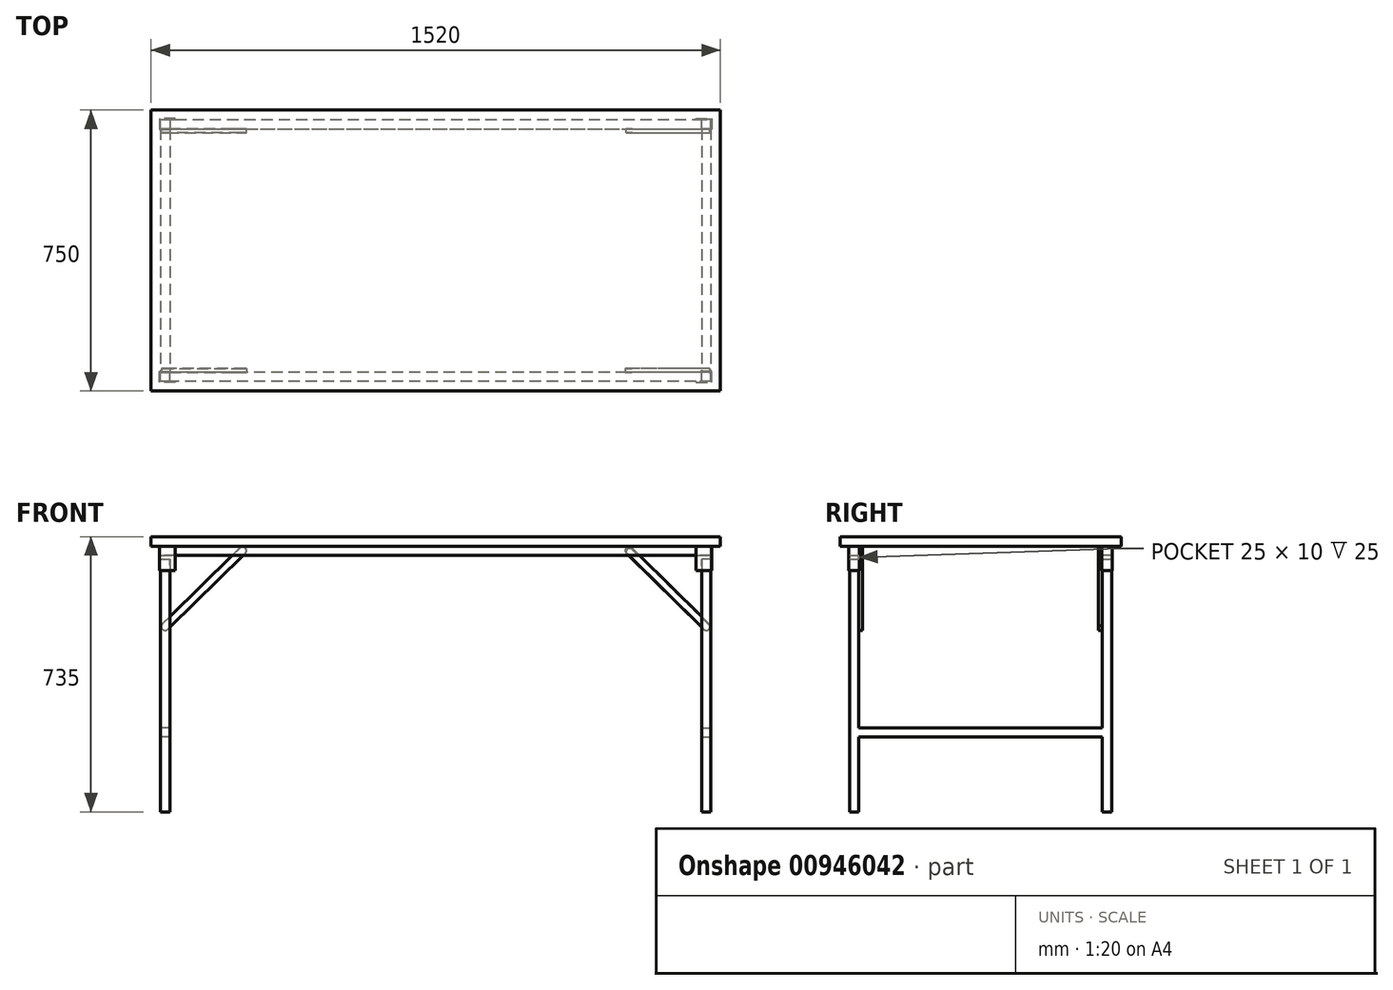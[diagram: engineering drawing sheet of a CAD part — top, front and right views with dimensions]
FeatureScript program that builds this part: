
annotation { "Feature Type Name" : "Feature", "Feature Type Description" : "" }
export const myFeature = defineFeature(function(context is Context, id is Id, definition is map)
    precondition{}
    {
        {
            var Q0;
            Q0=qCreatedBy(makeId("Top.planeOp"),FACE);
            var sketch = newSketch(context, id + "F0", { "sketchPlane" : qUnion([Q0])});
            skLineSegment(sketch, "E0.bottom", {"start": v(0, 0) * mm, "end": v(-1520, 0) * mm});
            skLineSegment(sketch, "E0.top", {"start": v(0, 750) * mm, "end": v(-1520, 750) * mm});
            skLineSegment(sketch, "E0.left", {"start": v(0, 0) * mm, "end": v(0, 750) * mm});
            skLineSegment(sketch, "E0.right", {"start": v(-1520, 0) * mm, "end": v(-1520, 750) * mm});
            skSolve(sketch);
        }
        {
            var Q0;
            Q0=makeQuery(id+"F0.imprint","IMPRINT",FACE,{"disambiguationData":[TD([[makeQuery(id+"F0.imprint","IMPRINT",EDGE,{"derivedFrom":sQuery(id+"F0.wireOp",EDGE,"E0.bottom")}),-1.0]])]});
            extrude(context, id + "F1", {"entities" : qUnion([Q0]), "depth" : 25 * mm, "offsetDistance" : 25 * mm});
        }
        {
            var Q0;
            Q0=makeQuery(id+"F1.opExtrude","CAP_FACE",FACE,{"disambiguationData":[OSD([sQuery(id+"F0.wireOp",EDGE,"E0.bottom"),sQuery(id+"F0.wireOp",EDGE,"E0.top"),sQuery(id+"F0.wireOp",EDGE,"E0.left"),sQuery(id+"F0.wireOp",EDGE,"E0.right")])],"isStart":true});
            var sketch = newSketch(context, id + "F2", { "sketchPlane" : qUnion([Q0])});
            skLineSegment(sketch, "E1.bottom", {"start": v(-25, -25) * mm, "end": v(-1495, -25) * mm});
            skLineSegment(sketch, "E1.top", {"start": v(-25, -50) * mm, "end": v(-1495, -50) * mm});
            skLineSegment(sketch, "E1.left", {"start": v(-25, -25) * mm, "end": v(-25, -50) * mm});
            skLineSegment(sketch, "E1.right", {"start": v(-1495, -25) * mm, "end": v(-1495, -50) * mm});
            skLineSegment(sketch, "E2.bottom", {"start": v(-1495, -700) * mm, "end": v(-25, -700) * mm});
            skLineSegment(sketch, "E2.top", {"start": v(-1495, -725) * mm, "end": v(-25, -725) * mm});
            skLineSegment(sketch, "E2.left", {"start": v(-1495, -700) * mm, "end": v(-1495, -725) * mm});
            skLineSegment(sketch, "E2.right", {"start": v(-25, -700) * mm, "end": v(-25, -725) * mm});
            skSolve(sketch);
        }
        {
            var Q0;
            Q0 = qSketchRegion(id + "F2", true);
            extrude(context, id + "F3", {"entities" : qUnion([Q0]), "operationType" : NewBodyOperationType.ADD, "depth" : 25 * mm, "offsetDistance" : 25 * mm});
        }
        {
            var Q0;
            Q0=makeQuery(id+"F1.opExtrude","CAP_FACE",FACE,{"disambiguationData":[OSD([sQuery(id+"F0.wireOp",EDGE,"E0.bottom"),sQuery(id+"F0.wireOp",EDGE,"E0.top"),sQuery(id+"F0.wireOp",EDGE,"E0.left"),sQuery(id+"F0.wireOp",EDGE,"E0.right")])],"isStart":true});
            var sketch = newSketch(context, id + "F4", { "sketchPlane" : qUnion([Q0])});
            skLineSegment(sketch, "E3", {"start": v(-25, -25) * mm, "end": v(-65, -25) * mm});
            skLineSegment(sketch, "E4", {"start": v(-65, -25) * mm, "end": v(-65, -23) * mm});
            skLineSegment(sketch, "E5", {"start": v(-65, -23) * mm, "end": v(-23, -23) * mm});
            skLineSegment(sketch, "E6", {"start": v(-23, -23) * mm, "end": v(-23, -52) * mm});
            skLineSegment(sketch, "E7", {"start": v(-23, -52) * mm, "end": v(-65, -52) * mm});
            skLineSegment(sketch, "E8", {"start": v(-65, -52) * mm, "end": v(-65, -50) * mm});
            skLineSegment(sketch, "E9", {"start": v(-65, -50) * mm, "end": v(-25, -50) * mm});
            skLineSegment(sketch, "E10", {"start": v(-25, -50) * mm, "end": v(-25, -25) * mm});
            skSolve(sketch);
        }
        {
            var Q0;
            Q0=makeQuery(id+"F4.imprint","IMPRINT",FACE,{"disambiguationData":[TD([[makeQuery(id+"F4.imprint","IMPRINT",EDGE,{"derivedFrom":sQuery(id+"F4.wireOp",EDGE,"E3")}),-1.0]])]});
            extrude(context, id + "F5", {"entities" : qUnion([Q0]), "operationType" : NewBodyOperationType.ADD, "depth" : 65 * mm, "offsetDistance" : 25 * mm});
        }
        {
            var Q0;
            Q0=makeQuery(id+"F3.opExtrude","CAP_FACE",FACE,{"disambiguationData":[OSD([sQuery(id+"F2.wireOp",EDGE,"E1.bottom"),sQuery(id+"F2.wireOp",EDGE,"E1.top"),sQuery(id+"F2.wireOp",EDGE,"E1.left"),sQuery(id+"F2.wireOp",EDGE,"E1.right")])],"isStart":false});
            cPlane(context, id + "F6", {"entities" : qUnion([Q0]), "cplaneType" : CPlaneType.OFFSET, "offset" : 10 * mm, "width" : 150 * mm, "height" : 150 * mm});
        }
        {
            var Q0;
            Q0=qCreatedBy(id+"F6.planeOp",FACE);
            var sketch = newSketch(context, id + "F7", { "sketchPlane" : qUnion([Q0])});
            skLineSegment(sketch, "E11.bottom", {"start": v(-25, -25.02) * mm, "end": v(-50, -25.02) * mm});
            skLineSegment(sketch, "E11.top", {"start": v(-25, -50.02) * mm, "end": v(-50, -50.02) * mm});
            skLineSegment(sketch, "E11.left", {"start": v(-25, -25.02) * mm, "end": v(-25, -50.02) * mm});
            skLineSegment(sketch, "E11.right", {"start": v(-50, -25.02) * mm, "end": v(-50, -50.02) * mm});
            skSolve(sketch);
        }
        {
            var Q0;
            Q0=makeQuery(id+"F7.imprint","IMPRINT",FACE,{"disambiguationData":[TD([[makeQuery(id+"F7.imprint","IMPRINT",EDGE,{"derivedFrom":sQuery(id+"F7.wireOp",EDGE,"E11.bottom")}),1.0]])]});
            extrude(context, id + "F8", {"entities" : qUnion([Q0]), "operationType" : NewBodyOperationType.ADD, "depth" : 675 * mm, "offsetDistance" : 25 * mm});
        }
        {
            var Q0;
            Q0=makeQuery(id+"F0.imprint","IMPRINT",FACE,{"disambiguationData":[TD([[makeQuery(id+"F0.imprint","IMPRINT",EDGE,{"derivedFrom":sQuery(id+"F0.wireOp",EDGE,"E0.bottom")}),-1.0]])]});
            var sketch = newSketch(context, id + "F9", { "sketchPlane" : qUnion([Q0])});
            skLineSegment(sketch, "E12", {"start": v(-1495, 25) * mm, "end": v(-1455, 25) * mm});
            skLineSegment(sketch, "E13", {"start": v(-1455, 25) * mm, "end": v(-1455, 23) * mm});
            skLineSegment(sketch, "E14", {"start": v(-1455, 23) * mm, "end": v(-1497, 23) * mm});
            skLineSegment(sketch, "E15", {"start": v(-1497, 23) * mm, "end": v(-1497, 52) * mm});
            skLineSegment(sketch, "E16", {"start": v(-1497, 52) * mm, "end": v(-1455, 52) * mm});
            skLineSegment(sketch, "E17", {"start": v(-1455, 52) * mm, "end": v(-1455, 50) * mm});
            skLineSegment(sketch, "E18", {"start": v(-1455, 50) * mm, "end": v(-1495, 50) * mm});
            skLineSegment(sketch, "E19", {"start": v(-1495, 50) * mm, "end": v(-1495, 25) * mm});
            skLineSegment(sketch, "E20.MirrorCS", {"start": v(-1455, 724.98) * mm, "end": v(-1455, 726.98) * mm});
            skLineSegment(sketch, "E21.MirrorCS", {"start": v(-1455, 697.98) * mm, "end": v(-1455, 699.98) * mm});
            skLineSegment(sketch, "E22.MirrorCS", {"start": v(-1497, 697.98) * mm, "end": v(-1455, 697.98) * mm});
            skLineSegment(sketch, "E23.MirrorCS", {"start": v(-1455, 699.98) * mm, "end": v(-1495, 699.98) * mm});
            skLineSegment(sketch, "E24.MirrorCS", {"start": v(-1495, 724.98) * mm, "end": v(-1455, 724.98) * mm});
            skLineSegment(sketch, "E25.MirrorCS", {"start": v(-1455, 726.98) * mm, "end": v(-1497, 726.98) * mm});
            skLineSegment(sketch, "E26.MirrorCS", {"start": v(-1497, 726.98) * mm, "end": v(-1497, 697.98) * mm});
            skLineSegment(sketch, "E27.MirrorCS", {"start": v(-1495, 699.98) * mm, "end": v(-1495, 724.98) * mm});
            skLineSegment(sketch, "E28.MirrorCS", {"start": v(-65.05, 724.98) * mm, "end": v(-65.05, 726.98) * mm});
            skLineSegment(sketch, "E29.MirrorCS", {"start": v(-65.05, 697.98) * mm, "end": v(-65.05, 699.98) * mm});
            skLineSegment(sketch, "E30.MirrorCS", {"start": v(-23.05, 726.98) * mm, "end": v(-23.05, 697.98) * mm});
            skLineSegment(sketch, "E31.MirrorCS", {"start": v(-65.05, 699.98) * mm, "end": v(-25.05, 699.98) * mm});
            skLineSegment(sketch, "E32.MirrorCS", {"start": v(-25.05, 699.98) * mm, "end": v(-25.05, 724.98) * mm});
            skLineSegment(sketch, "E33.MirrorCS", {"start": v(-65.05, 726.98) * mm, "end": v(-23.05, 726.98) * mm});
            skLineSegment(sketch, "E34.MirrorCS", {"start": v(-25.05, 724.98) * mm, "end": v(-65.05, 724.98) * mm});
            skLineSegment(sketch, "E35.MirrorCS", {"start": v(-23.05, 697.98) * mm, "end": v(-65.05, 697.98) * mm});
            skSolve(sketch);
        }
        {
            var Q0;
            Q0=makeQuery(id+"F9.imprint","IMPRINT",FACE,{"disambiguationData":[TD([[makeQuery(id+"F9.imprint","IMPRINT",EDGE,{"derivedFrom":sQuery(id+"F9.wireOp",EDGE,"E20.MirrorCS")}),1.0]])]});
            var Q1;
            Q1=makeQuery(id+"F9.imprint","IMPRINT",FACE,{"disambiguationData":[TD([[makeQuery(id+"F9.imprint","IMPRINT",EDGE,{"derivedFrom":sQuery(id+"F9.wireOp",EDGE,"E28.MirrorCS")}),-1.0]])]});
            var Q2;
            Q2=makeQuery(id+"F9.imprint","IMPRINT",FACE,{"disambiguationData":[TD([[makeQuery(id+"F9.imprint","IMPRINT",EDGE,{"derivedFrom":sQuery(id+"F9.wireOp",EDGE,"E12")}),-1.0]])]});
            extrude(context, id + "F10", {"entities" : qUnion([Q0, Q1, Q2]), "operationType" : NewBodyOperationType.ADD, "oppositeDirection" : true, "depth" : 65 * mm, "offsetDistance" : 25 * mm});
        }
        {
            var Q0;
            Q0=makeQuery(id+"F3.opExtrude","CAP_FACE",FACE,{"disambiguationData":[OSD([sQuery(id+"F2.wireOp",EDGE,"E1.bottom"),sQuery(id+"F2.wireOp",EDGE,"E1.top"),sQuery(id+"F2.wireOp",EDGE,"E1.left"),sQuery(id+"F2.wireOp",EDGE,"E1.right")])],"isStart":false});
            cPlane(context, id + "F11", {"entities" : qUnion([Q0]), "cplaneType" : CPlaneType.OFFSET, "offset" : 10 * mm, "width" : 150 * mm, "height" : 150 * mm});
        }
        {
            var Q0;
            Q0=qCreatedBy(id+"F11.planeOp",FACE);
            var sketch = newSketch(context, id + "F12", { "sketchPlane" : qUnion([Q0])});
            skLineSegment(sketch, "E36.bottom", {"start": v(-1470, -25) * mm, "end": v(-1495, -25) * mm});
            skLineSegment(sketch, "E36.top", {"start": v(-1470, -50) * mm, "end": v(-1495, -50) * mm});
            skLineSegment(sketch, "E36.left", {"start": v(-1470, -25) * mm, "end": v(-1470, -50) * mm});
            skLineSegment(sketch, "E36.right", {"start": v(-1495, -25) * mm, "end": v(-1495, -50) * mm});
            skSolve(sketch);
        }
        {
            var Q0;
            Q0=makeQuery(id+"F12.imprint","IMPRINT",FACE,{"disambiguationData":[TD([[makeQuery(id+"F12.imprint","IMPRINT",EDGE,{"derivedFrom":sQuery(id+"F12.wireOp",EDGE,"E36.bottom")}),1.0]])]});
            extrude(context, id + "F13", {"entities" : qUnion([Q0]), "operationType" : NewBodyOperationType.ADD, "depth" : 675 * mm, "offsetDistance" : 25 * mm});
        }
        {
            var Q0;
            Q0=makeQuery(id+"F3.opExtrude","CAP_FACE",FACE,{"disambiguationData":[OSD([sQuery(id+"F2.wireOp",EDGE,"E2.bottom"),sQuery(id+"F2.wireOp",EDGE,"E2.top"),sQuery(id+"F2.wireOp",EDGE,"E2.left"),sQuery(id+"F2.wireOp",EDGE,"E2.right")])],"isStart":false});
            cPlane(context, id + "F14", {"entities" : qUnion([Q0]), "cplaneType" : CPlaneType.OFFSET, "offset" : 10 * mm, "width" : 150 * mm, "height" : 150 * mm});
        }
        {
            var Q0;
            Q0=qCreatedBy(id+"F14.planeOp",FACE);
            var sketch = newSketch(context, id + "F15", { "sketchPlane" : qUnion([Q0])});
            skLineSegment(sketch, "E37.bottom", {"start": v(-25, -700) * mm, "end": v(-50, -700) * mm});
            skLineSegment(sketch, "E37.top", {"start": v(-25, -725) * mm, "end": v(-50, -725) * mm});
            skLineSegment(sketch, "E37.left", {"start": v(-25, -700) * mm, "end": v(-25, -725) * mm});
            skLineSegment(sketch, "E37.right", {"start": v(-50, -700) * mm, "end": v(-50, -725) * mm});
            skLineSegment(sketch, "E38.bottom", {"start": v(-1495, -725) * mm, "end": v(-1470, -725) * mm});
            skLineSegment(sketch, "E38.top", {"start": v(-1495, -700) * mm, "end": v(-1470, -700) * mm});
            skLineSegment(sketch, "E38.left", {"start": v(-1495, -725) * mm, "end": v(-1495, -700) * mm});
            skLineSegment(sketch, "E38.right", {"start": v(-1470, -725) * mm, "end": v(-1470, -700) * mm});
            skSolve(sketch);
        }
        {
            var Q0;
            Q0 = qSketchRegion(id + "F15", true);
            extrude(context, id + "F16", {"entities" : qUnion([Q0]), "operationType" : NewBodyOperationType.ADD, "depth" : 675 * mm, "offsetDistance" : 25 * mm});
        }
        {
            var Q0;
            Q0=makeQuery(id+"F8.opExtrude","SWEPT_FACE",FACE,{"disambiguationData":[OSD([sQuery(id+"F7.wireOp",EDGE,"E11.top")])]});
            cPlane(context, id + "F17", {"entities" : qUnion([Q0]), "cplaneType" : CPlaneType.OFFSET, "offset" : 0 * mm, "width" : 150 * mm, "height" : 150 * mm});
        }
        {
            var Q0;
            Q0=qCreatedBy(id+"F17.planeOp",FACE);
            var sketch = newSketch(context, id + "F18", { "sketchPlane" : qUnion([Q0])});
            skLineSegment(sketch, "E39.bottom", {"start": v(25, -485) * mm, "end": v(50, -485) * mm});
            skLineSegment(sketch, "E39.top", {"start": v(25, -510) * mm, "end": v(50, -510) * mm});
            skLineSegment(sketch, "E39.left", {"start": v(25, -485) * mm, "end": v(25, -510) * mm});
            skLineSegment(sketch, "E39.right", {"start": v(50, -485) * mm, "end": v(50, -510) * mm});
            skSolve(sketch);
        }
        {
            var Q0;
            Q0=makeQuery(id+"F18.imprint","IMPRINT",FACE,{"disambiguationData":[TD([[makeQuery(id+"F18.imprint","IMPRINT",EDGE,{"derivedFrom":sQuery(id+"F18.wireOp",EDGE,"E39.bottom")}),-1.0]])]});
            extrude(context, id + "F19", {"entities" : qUnion([Q0]), "operationType" : NewBodyOperationType.ADD, "depth" : 650 * mm, "offsetDistance" : 25 * mm});
        }
        {
            var Q0;
            Q0=makeQuery(id+"F13.opExtrude","SWEPT_FACE",FACE,{"disambiguationData":[OSD([sQuery(id+"F12.wireOp",EDGE,"E36.top")])]});
            cPlane(context, id + "F20", {"entities" : qUnion([Q0]), "cplaneType" : CPlaneType.OFFSET, "offset" : 0 * mm, "width" : 150 * mm, "height" : 150 * mm});
        }
        {
            var Q0;
            Q0=qCreatedBy(id+"F20.planeOp",FACE);
            var sketch = newSketch(context, id + "F21", { "sketchPlane" : qUnion([Q0])});
            skLineSegment(sketch, "E40.0", {"start": v(1470, -710) * mm, "end": v(1470, -65) * mm});
            skLineSegment(sketch, "E41.0.0", {"start": v(1495, -65) * mm, "end": v(1470, -65) * mm});
            skLineSegment(sketch, "E41.0.1", {"start": v(1470, -65) * mm, "end": v(1470, -710) * mm});
            skLineSegment(sketch, "E41.0.2", {"start": v(1470, -710) * mm, "end": v(1495, -710) * mm});
            skLineSegment(sketch, "E41.0.3", {"start": v(1495, -710) * mm, "end": v(1495, -65) * mm});
            skLineSegment(sketch, "E42.bottom", {"start": v(1470, -485) * mm, "end": v(1495, -485) * mm});
            skLineSegment(sketch, "E42.top", {"start": v(1470, -510) * mm, "end": v(1495, -510) * mm});
            skLineSegment(sketch, "E42.left", {"start": v(1470, -485) * mm, "end": v(1470, -510) * mm});
            skLineSegment(sketch, "E42.right", {"start": v(1495, -485) * mm, "end": v(1495, -510) * mm});
            skSolve(sketch);
        }
        {
            var Q0;
            Q0=makeQuery(id+"F21.imprint","IMPRINT",FACE,{"disambiguationData":[TD([[makeQuery(id+"F21.imprint","IMPRINT",EDGE,{"derivedFrom":sQuery(id+"F21.wireOp",EDGE,"E42.bottom")}),-1.0]])]});
            extrude(context, id + "F22", {"entities" : qUnion([Q0]), "operationType" : NewBodyOperationType.ADD, "depth" : 650 * mm, "offsetDistance" : 25 * mm});
        }
        {
            var Q0;
            {var subQ0=sQuery(id+"F9.wireOp",EDGE,"E32.MirrorCS");var subQ3=sQuery(id+"F15.wireOp",EDGE,"E37.bottom");Q0=makeQuery(id+"F19.boolean.opBoolean","SPLIT",FACE,{"disambiguationData":[TD([makeQuery(id+"F10.opExtrude","SWEPT_FACE",FACE,{"disambiguationData":[OSD([subQ0])]})])],"derivedFrom":makeQuery(id+"F16.opExtrude","SWEPT_FACE",FACE,{"disambiguationData":[OSD([subQ3])]})});}
            var sketch = newSketch(context, id + "F23", { "sketchPlane" : qUnion([Q0])});
            skPoint(sketch, "E43", {"position": v(-37.5, -215) * mm});
            skPoint(sketch, "E44", {"position": v(-243.05, -12.5) * mm});
            skPoint(sketch, "E45", {"position": v(-118.3, 56.79) * mm});
            skLineSegment(sketch, "E46", {"start": v(-234.62, -9.28) * mm, "end": v(-27.8, -212.56) * mm});
            skLineSegment(sketch, "E47", {"start": v(-251.33, -18.85) * mm, "end": v(-44.5, -222.13) * mm});
            skArc(sketch, "E48", {"start": v(-44.5, -222.13) * mm, "mid": v(-32.53, -223.68) * mm, "end": v(-27.8, -212.56) * mm});
            skArc(sketch, "E49", {"start": v(-234.62, -9.28) * mm, "mid": v(-246.6, -7.73) * mm, "end": v(-251.33, -18.85) * mm});
            skSolve(sketch);
        }
        {
            var Q0;
            {var subQ0=sQuery(id+"F23.wireOp",EDGE,"E49");Q0=makeQuery(id+"F23.imprint","IMPRINT",FACE,{"disambiguationData":[TD([[makeQuery(id+"F23.imprint","IMPRINT",EDGE,{"derivedFrom":subQ0}),1.0]])]});}
            var Q1;
            {var subQ0=sQuery(id+"F23.wireOp",EDGE,"E48");Q1=makeQuery(id+"F23.imprint","IMPRINT",FACE,{"disambiguationData":[TD([[makeQuery(id+"F23.imprint","IMPRINT",EDGE,{"derivedFrom":subQ0}),1.0]])]});}
            extrude(context, id + "F24", {"entities" : qUnion([Q0, Q1]), "operationType" : NewBodyOperationType.ADD, "depth" : 10 * mm, "offsetDistance" : 25 * mm});
        }
        {
            var Q0;
            Q0=makeQuery(id+"F19.boolean.opBoolean","SPLIT",FACE,{"disambiguationData":[TD([makeQuery(id+"F19.opExtrude","SWEPT_FACE",FACE,{"disambiguationData":[OSD([sQuery(id+"F18.wireOp",EDGE,"E39.bottom")])]})])],"derivedFrom":makeQuery(id+"F8.opExtrude","SWEPT_FACE",FACE,{"disambiguationData":[OSD([sQuery(id+"F7.wireOp",EDGE,"E11.top")])]})});
            var sketch = newSketch(context, id + "F25", { "sketchPlane" : qUnion([Q0])});
            skPoint(sketch, "E50", {"position": v(37.5, -215) * mm});
            skPoint(sketch, "E51", {"position": v(243, -12.5) * mm});
            skLineSegment(sketch, "E52", {"start": v(44.52, -222.12) * mm, "end": v(250.98, -18.46) * mm});
            skLineSegment(sketch, "E53", {"start": v(30.48, -207.88) * mm, "end": v(236.93, -4.22) * mm});
            skLineSegment(sketch, "E54", {"start": v(43.27, -207.6) * mm, "end": v(43.27, -207.6) * mm});
            skArc(sketch, "E55", {"start": v(30.48, -207.88) * mm, "mid": v(30.38, -222.02) * mm, "end": v(44.52, -222.12) * mm});
            skArc(sketch, "E56", {"start": v(250.98, -18.46) * mm, "mid": v(251.08, -4.32) * mm, "end": v(236.93, -4.22) * mm});
            skSolve(sketch);
        }
        {
            var Q0;
            {var subQ0=sQuery(id+"F25.wireOp",EDGE,"E56");Q0=makeQuery(id+"F25.imprint","IMPRINT",FACE,{"disambiguationData":[TD([[makeQuery(id+"F25.imprint","IMPRINT",EDGE,{"derivedFrom":subQ0}),1.0]])]});}
            var Q1;
            {var subQ0=sQuery(id+"F25.wireOp",EDGE,"E55");Q1=makeQuery(id+"F25.imprint","IMPRINT",FACE,{"disambiguationData":[TD([[makeQuery(id+"F25.imprint","IMPRINT",EDGE,{"derivedFrom":subQ0}),1.0]])]});}
            extrude(context, id + "F26", {"entities" : qUnion([Q0, Q1]), "depth" : 10 * mm, "offsetDistance" : 25 * mm});
        }
        {
            var Q0;
            {var subQ2=sQuery(id+"F15.wireOp",EDGE,"E38.top");var subQ3=sQuery(id+"F9.wireOp",EDGE,"E27.MirrorCS");Q0=makeQuery(id+"F22.boolean.opBoolean","SPLIT",FACE,{"disambiguationData":[TD([makeQuery(id+"F10.opExtrude","SWEPT_FACE",FACE,{"disambiguationData":[OSD([subQ3])]})])],"derivedFrom":makeQuery(id+"F16.opExtrude","SWEPT_FACE",FACE,{"disambiguationData":[OSD([subQ2])]})});}
            cPlane(context, id + "F27", {"entities" : qUnion([Q0]), "cplaneType" : CPlaneType.OFFSET, "offset" : 0 * mm, "width" : 150 * mm, "height" : 150 * mm});
        }
        {
            var Q0;
            Q0=qCreatedBy(id+"F27.planeOp",FACE);
            var sketch = newSketch(context, id + "F28", { "sketchPlane" : qUnion([Q0])});
            skPoint(sketch, "E57", {"position": v(-1482.5, -215) * mm});
            skPoint(sketch, "E58", {"position": v(-1277, -12.5) * mm});
            skLineSegment(sketch, "E59", {"start": v(-1282.53, -4.73) * mm, "end": v(-1489.5, -207.86) * mm});
            skLineSegment(sketch, "E60", {"start": v(-1475.5, -222.14) * mm, "end": v(-1268.52, -19) * mm});
            skArc(sketch, "E61", {"start": v(-1489.5, -207.86) * mm, "mid": v(-1489.64, -222) * mm, "end": v(-1475.5, -222.14) * mm});
            skArc(sketch, "E62", {"start": v(-1268.52, -19) * mm, "mid": v(-1268.39, -4.87) * mm, "end": v(-1282.53, -4.73) * mm});
            skSolve(sketch);
        }
        {
            var Q0;
            Q0=makeQuery(id+"F28.imprint","IMPRINT",FACE,{"disambiguationData":[TD([[makeQuery(id+"F28.imprint","IMPRINT",EDGE,{"derivedFrom":sQuery(id+"F28.wireOp",EDGE,"E59")}),1.0]])]});
            extrude(context, id + "F29", {"entities" : qUnion([Q0]), "operationType" : NewBodyOperationType.ADD, "depth" : 10 * mm, "offsetDistance" : 25 * mm});
        }
        {
            var Q0;
            {var subQ0=sQuery(id+"F21.wireOp",EDGE,"E41.0.0");Q0=makeQuery(id+"F21.imprint","IMPRINT",FACE,{"disambiguationData":[TD([[makeQuery(id+"F21.imprint","IMPRINT",EDGE,{"derivedFrom":subQ0}),1.0]])]});}
            var sketch = newSketch(context, id + "F30", { "sketchPlane" : qUnion([Q0])});
            skLineSegment(sketch, "E63", {"start": v(1489.5, -207.85) * mm, "end": v(1282.21, -5.04) * mm});
            skLineSegment(sketch, "E64", {"start": v(1268.23, -19.33) * mm, "end": v(1475.5, -222.15) * mm});
            skArc(sketch, "E65", {"start": v(1475.5, -222.15) * mm, "mid": v(1489.65, -222) * mm, "end": v(1489.5, -207.85) * mm});
            skArc(sketch, "E66", {"start": v(1282.21, -5.04) * mm, "mid": v(1268.07, -5.19) * mm, "end": v(1268.23, -19.33) * mm});
            skSolve(sketch);
        }
        {
            var Q0;
            {var subQ0=sQuery(id+"F30.wireOp",EDGE,"E65");Q0=makeQuery(id+"F30.imprint","IMPRINT",FACE,{"disambiguationData":[TD([[makeQuery(id+"F30.imprint","IMPRINT",EDGE,{"derivedFrom":subQ0}),1.0]])]});}
            var Q1;
            {var subQ0=sQuery(id+"F30.wireOp",EDGE,"E66");Q1=makeQuery(id+"F30.imprint","IMPRINT",FACE,{"disambiguationData":[TD([[makeQuery(id+"F30.imprint","IMPRINT",EDGE,{"derivedFrom":subQ0}),1.0]])]});}
            extrude(context, id + "F31", {"entities" : qUnion([Q0, Q1]), "operationType" : NewBodyOperationType.ADD, "depth" : 10 * mm, "offsetDistance" : 25 * mm});
        }
    });
